# Revit family: Drain_Floor_Medium-Depth_Round_Zurn-Z1731_Heavy-Duty
name_source: partatom
category: Plumbing Fixtures
units: mm (PartAtom-declared; Revit-internal decimal feet)

## family parameters
Always vertical = Yes
Cut with Voids When Loaded = No
Maintain Annotation Orientation = No
OmniClass Number = 23.45.55.21
OmniClass Title = Drains (Wastes)
Part Type = Normal
Room Calculation Point = No
Round Connector Dimension = Use Radius
Shared = No
Work Plane-Based = No

## types (16) — shared parameters
Approx. Weight (Lbs) = 22 "
Assembly Code = D2030300
Body HT Dim 'E' = 5.688 "
CW Connection = No
Description = 9 INCH DIAMETER FLOOR DRAIN MEDIUM DEPTH
HW Connection = No
Manufacturer = Zurn Water, LLC
Manufacurer Brand = Zurn
Modified Date = 10/31/25
Product Documentation Link = https://files.zurn.com
Product Page URL = https://www.zurn.com
Product data url = https://www.bimobject.com
URL = www.zurn.com
Vent Connection = No
Waste Connection = Yes
zero-valued in all types: CWFU, Default Elevation, HWFU, WFU

## per-type parameters (varying)
| type | Main Material | Model | Pipe Size 'A' (Inner Diameter) | Pipe Size 'A' (Inner Radius) | Pipe Size 'A' (Nominal Diameter) | Pipe Size 'A' (Nominal Radius) | Pipe Size 'A' (Outer Diameter) | Pipe Size 'A' (Outer Radius) | Type Comments |
| Z1731-3BW | Steel - Zurn- Stainless - Type - 304 | Z1731 | 3.068 " | 1.534 " | 3 " | 1.5 " | 3.5 " | 1.75 " | Z1731 - 3 inch Butt-Weld Outlet |
| Z1731-4BW | Steel - Zurn- Stainless - Type - 304 | Z1731 | 4.026 " | 2.013 " | 4 " | 2 " | 4.5 " | 2.25 " | Z1731 - 4 inch Butt-Weld Outlet |
| Z1731-3IC | Steel - Zurn- Stainless - Type - 304 | Z1731 | 3.068 " | 1.534 " | 3 " | 1.5 " | 3.5 " | 1.75 " | Z1731 - 3 inch Inside Caulk Outlet |
| Z1731-4IC | Steel - Zurn- Stainless - Type - 304 | Z1731 | 4.026 " | 2.013 " | 4 " | 2 " | 4.5 " | 2.25 " | Z1731 - 4 inch Inside Caulk Outlet |
| Z1731-3IP | Steel - Zurn- Stainless - Type - 304 | Z1731 | 3.068 " | 1.534 " | 3 " | 1.5 " | 3.5 " | 1.75 " | Z1731 - 3 inch IP Threaded Outlet |
| Z1731-4IP | Steel - Zurn- Stainless - Type - 304 | Z1731 | 4.026 " | 2.013 " | 4 " | 2 " | 4.5 " | 2.25 " | Z1731 - 4 inch IP Threaded Outlet |
| Z1731-3NH | Steel - Zurn- Stainless - Type - 304 | Z1731 | 3.068 " | 1.534 " | 3 " | 1.5 " | 3.5 " | 1.75 " | Z1731 - 3 inch No-Hub Outlet |
| Z1731-4NH | Steel - Zurn- Stainless - Type - 304 | Z1731 | 4.026 " | 2.013 " | 4 " | 2 " | 4.5 " | 2.25 " | Z1731 - 4 inch No-Hub Outlet |
| ZM1731-3BW | Steel - Zurn- Stainless - Type - 316 | ZM1731 | 3.068 " | 1.534 " | 3 " | 1.5 " | 3.5 " | 1.75 " | ZM1731 - 3 inch Butt-Weld Outlet |
| ZM1731-4BW | Steel - Zurn- Stainless - Type - 316 | ZM1731 | 4.026 " | 2.013 " | 4 " | 2 " | 4.5 " | 2.25 " | ZM1731 - 4 inch Butt-Weld Outlet |
| ZM1731-3IC | Steel - Zurn- Stainless - Type - 316 | ZM1731 | 3.068 " | 1.534 " | 3 " | 1.5 " | 3.5 " | 1.75 " | ZM1731 - 3 inch Inside Caulk Outlet |
| ZM1731-4IC | Steel - Zurn- Stainless - Type - 316 | ZM1731 | 4.026 " | 2.013 " | 4 " | 2 " | 4.5 " | 2.25 " | ZM1731 - 4 inch Inside Caulk Outlet |
| ZM1731-3IP | Steel - Zurn- Stainless - Type - 316 | ZM1731 | 3.068 " | 1.534 " | 3 " | 1.5 " | 3.5 " | 1.75 " | ZM1731 - 3 inch IP Threaded Outlet |
| ZM1731-4IP | Steel - Zurn- Stainless - Type - 316 | ZM1731 | 4.026 " | 2.013 " | 4 " | 2 " | 4.5 " | 2.25 " | ZM1731 - 4 inch IP Threaded Outlet |
| ZM1731-3NH | Steel - Zurn- Stainless - Type - 316 | ZM1731 | 3.068 " | 1.534 " | 3 " | 1.5 " | 3.5 " | 1.75 " | ZM1731 - 3 inch No-Hub Outlet |
| ZM1731-4NH | Steel - Zurn- Stainless - Type - 316 | ZM1731 | 4.026 " | 2.013 " | 4 " | 2 " | 4.5 " | 2.25 " | ZM1731 - 4 inch No-Hub Outlet |

## geometry (parser evidence)
native form markers: Sweep x4
no freeform markers — native parametric forms only
